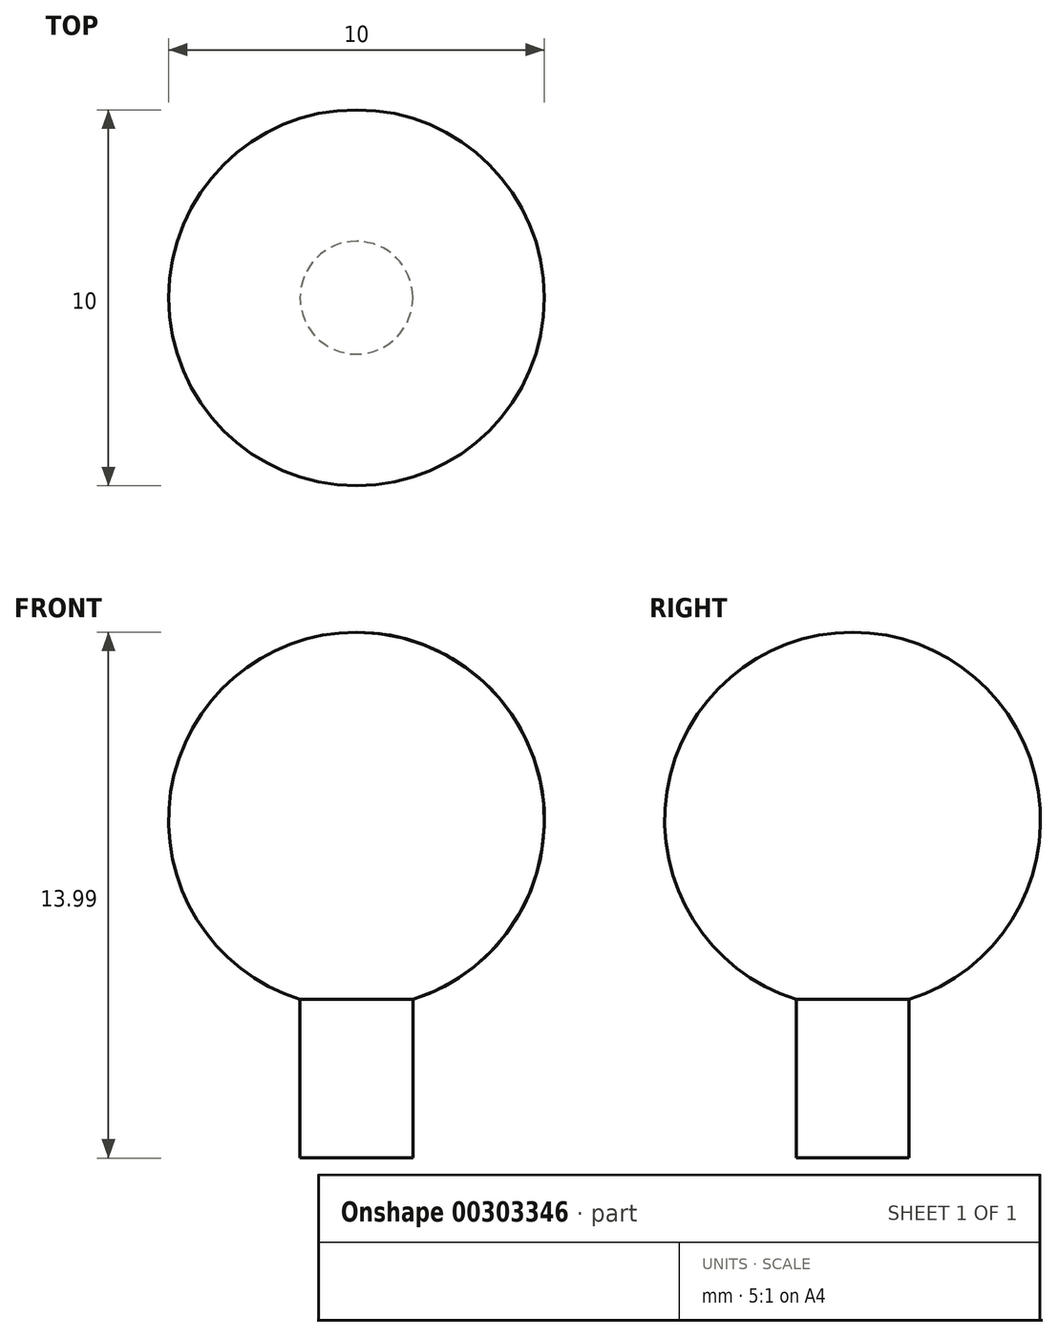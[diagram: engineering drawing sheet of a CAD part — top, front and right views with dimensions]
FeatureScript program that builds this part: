
annotation { "Feature Type Name" : "Feature", "Feature Type Description" : "" }
export const myFeature = defineFeature(function(context is Context, id is Id, definition is map)
    precondition{}
    {
        {
            var Q0;
            Q0=qCreatedBy(makeId("Front.planeOp"),FACE);
            var sketch = newSketch(context, id + "F0", { "sketchPlane" : qUnion([Q0])});
            skArc(sketch, "E0", {"start": v(1.5, -4.77) * mm, "mid": v(4.94, 0.76) * mm, "end": v(0, 5) * mm});
            skLineSegment(sketch, "E1.top", {"start": v(0, -8.99) * mm, "end": v(1.5, -8.99) * mm});
            skLineSegment(sketch, "E1.right", {"start": v(1.5, -4.77) * mm, "end": v(1.5, -8.99) * mm});
            skLineSegment(sketch, "E2", {"start": v(0, 5) * mm, "end": v(0, -8.99) * mm});
            skPoint(sketch, "E3.orphan", {"position": v(-1.5, -8.99) * mm});
            skSolve(sketch);
        }
        {
            var Q0;
            Q0=makeQuery(id+"F0.imprint","IMPRINT",FACE,{"disambiguationData":[TD([[makeQuery(id+"F0.imprint","IMPRINT",EDGE,{"derivedFrom":sQuery(id+"F0.wireOp",EDGE,"E0")}),1.0]])]});
            var Q1;
            Q1=sQuery(id+"F0.wireOp",EDGE,"E2");
            revolve(context, id + "F1", {"entities" : qUnion([Q0]), "axis" : qUnion([Q1]), "revolveType" : RevolveType.FULL});
        }
    });
